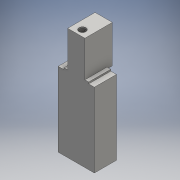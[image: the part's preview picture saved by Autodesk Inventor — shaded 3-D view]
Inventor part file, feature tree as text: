
AUTODESK INVENTOR PART (.ipt)
format: ipt  version: 2016 SP1 (Build 200210100, 210)  size: 457,728 bytes
history: native  units: mm
features: extrude x24, sketch x24, other x1
ambient origin geometry x8: Origin, YZ Plane, XZ Plane, XY Plane, X Axis, Y Axis, Z Axis, Center Point
bodies: Body1 (feature_tree)
feature tree (49):
  other  "Bryła1"
  extrude  "Wyciągnięcie proste1"  Depth=30.6mm
  extrude  "Wyciągnięcie proste2"  Depth=65.6mm
  extrude  "Wyciągnięcie proste3"  Depth=1.5mm TaperAngle=0.0deg
  extrude  "Wyciągnięcie proste4"  Depth=3.5mm
  extrude  "Wyciągnięcie proste5"  Depth=3.5mm
  extrude  "Wyciągnięcie proste6"  Depth=3.5mm
  extrude  "Wyciągnięcie proste7"  Depth=3.5mm
  extrude  "Wyciągnięcie proste8"  Depth=3.5mm
  extrude  "Wyciągnięcie proste9"  Depth=3.5mm
  extrude  "Wyciągnięcie proste10"  Depth=3.5mm
  extrude  "Wyciągnięcie proste11"  Depth=3.5mm
  extrude  "Wyciągnięcie proste12"  Depth=6.8mm
  extrude  "Wyciągnięcie proste13"  Depth=6.8mm
  extrude  "Wyciągnięcie proste14"  Depth=6.8mm
  extrude  "Wyciągnięcie proste15"  Depth=6.8mm
  extrude  "Wyciągnięcie proste16"  Depth=1.5mm TaperAngle=0.0deg
  extrude  "Wyciągnięcie proste17"  Depth=2.5mm
  extrude  "Wyciągnięcie proste18"  Depth=2.5mm
  extrude  "Wyciągnięcie proste19"  Depth=2.5mm
  extrude  "Wyciągnięcie proste20"  Depth=2.5mm
  extrude  "Wyciągnięcie proste21"  Depth=2.0mm TaperAngle=0.0deg
  extrude  "Wyciągnięcie proste22"  Depth=10.0mm
  extrude  "Wyciągnięcie proste23"  Depth=20.0mm
  extrude  "Wyciągnięcie proste24"  Depth=2.0mm
  sketch  "Szkic1"
  sketch  "Szkic2"
  sketch  "Szkic3"
  sketch  "Szkic4"
  sketch  "Szkic6"
  sketch  "Szkic7"
  sketch  "Szkic8"
  sketch  "Szkic9"
  sketch  "Szkic10"
  sketch  "Szkic11"
  sketch  "Szkic12"
  sketch  "Szkic13"
  sketch  "Szkic14"
  sketch  "Szkic15"
  sketch  "Szkic16"
  sketch  "Szkic18"
  sketch  "Szkic19"
  sketch  "Szkic20"
  sketch  "Szkic21"
  sketch  "Szkic22"
  sketch  "Szkic23"
  sketch  "Szkic24"
  sketch  "Szkic25"
  sketch  "Szkic26"
